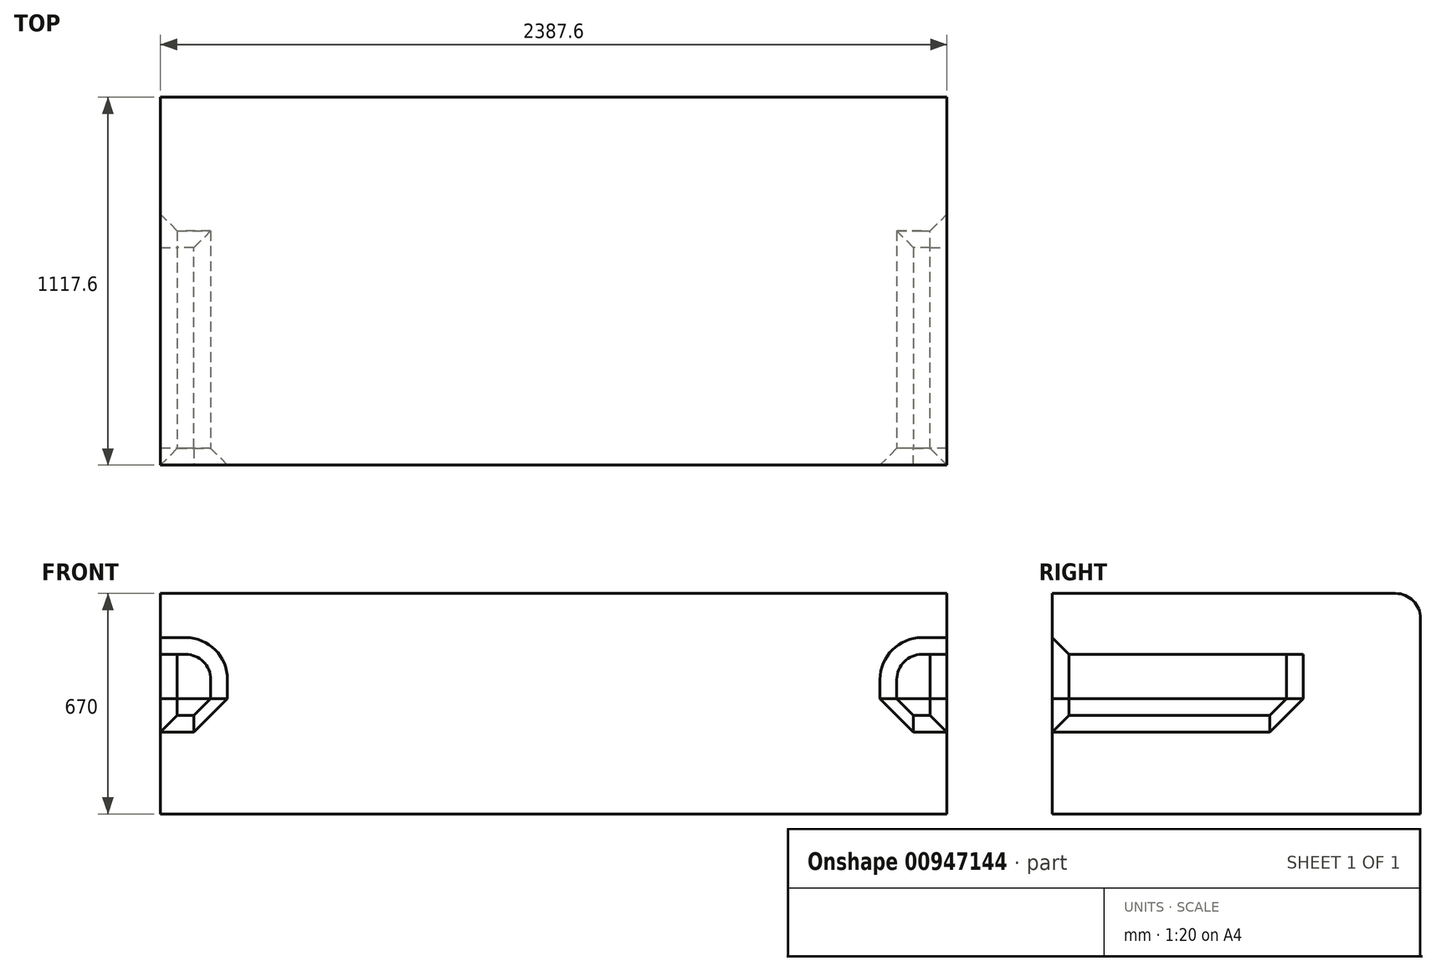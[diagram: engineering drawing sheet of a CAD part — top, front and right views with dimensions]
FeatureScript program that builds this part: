
annotation { "Feature Type Name" : "Feature", "Feature Type Description" : "" }
export const myFeature = defineFeature(function(context is Context, id is Id, definition is map)
    precondition{}
    {
        {
            var Q0;
            Q0=qCreatedBy(makeId("Top.planeOp"),FACE);
            var sketch = newSketch(context, id + "F0", { "sketchPlane" : qUnion([Q0])});
            skLineSegment(sketch, "E0.bottom", {"start": v(0, 0) * mm, "end": v(-2387.6, 0) * mm});
            skLineSegment(sketch, "E0.top", {"start": v(0, 1117.6) * mm, "end": v(-2387.6, 1117.6) * mm});
            skLineSegment(sketch, "E0.left", {"start": v(0, 0) * mm, "end": v(0, 1117.6) * mm});
            skLineSegment(sketch, "E0.right", {"start": v(-2387.6, 0) * mm, "end": v(-2387.6, 1117.6) * mm});
            skSolve(sketch);
        }
        {
            var Q0;
            Q0 = qSketchRegion(id + "F0", true);
            extrude(context, id + "F1", {"entities" : qUnion([Q0]), "flatOperationType" : FlatOperationType.REMOVE, "depth" : 670 * mm, "offsetDistance" : 25.4 * mm, "domain" : OperationDomain.MODEL});
        }
        {
            var Q0;
            Q0=makeQuery(id+"F1.opExtrude","SWEPT_FACE",FACE,{"disambiguationData":[OSD([sQuery(id+"F0.wireOp",EDGE,"E0.bottom")])]});
            var sketch = newSketch(context, id + "F2", { "sketchPlane" : qUnion([Q0])});
            skLineSegment(sketch, "E1.bottom", {"start": v(0, 300) * mm, "end": v(-2387.6, 300) * mm});
            skLineSegment(sketch, "E1.top", {"start": v(0, 670) * mm, "end": v(-2387.6, 670) * mm});
            skLineSegment(sketch, "E1.left", {"start": v(0, 300) * mm, "end": v(0, 670) * mm});
            skLineSegment(sketch, "E1.right", {"start": v(-2387.6, 300) * mm, "end": v(-2387.6, 670) * mm});
            skLineSegment(sketch, "E2.bottom", {"start": v(-2387.6, 670) * mm, "end": v(-2235.2, 670) * mm});
            skLineSegment(sketch, "E2.top", {"start": v(-2387.6, 300) * mm, "end": v(-2235.2, 300) * mm});
            skLineSegment(sketch, "E2.left", {"start": v(-2387.6, 670) * mm, "end": v(-2387.6, 300) * mm});
            skLineSegment(sketch, "E2.right", {"start": v(-2235.2, 485) * mm, "end": v(-2235.2, 300) * mm});
            skLineSegment(sketch, "E3.bottom", {"start": v(0, 670) * mm, "end": v(-152.4, 670) * mm});
            skLineSegment(sketch, "E3.top", {"start": v(0, 300) * mm, "end": v(-152.4, 300) * mm});
            skLineSegment(sketch, "E3.left", {"start": v(0, 670) * mm, "end": v(0, 300) * mm});
            skLineSegment(sketch, "E3.right", {"start": v(-152.4, 485) * mm, "end": v(-152.4, 300) * mm});
            skLineSegment(sketch, "E4", {"start": v(-2387.6, 485) * mm, "end": v(-2235.2, 485) * mm});
            skLineSegment(sketch, "E5", {"start": v(-152.4, 485) * mm, "end": v(0, 485) * mm});
            skSolve(sketch);
        }
        {
            var Q0;
            Q0=makeQuery(id+"F2.imprint","IMPRINT",FACE,{"disambiguationData":[TD([[makeQuery(id+"F2.imprint","IMPRINT",EDGE,{"derivedFrom":sQuery(id+"F2.wireOp",EDGE,"E1.bottom")}),-1.0]])]});
            extrude(context, id + "F3", {"entities" : qUnion([Q0]), "operationType" : NewBodyOperationType.REMOVE, "oppositeDirection" : true, "depth" : 711.2 * mm, "offsetDistance" : 25.4 * mm});
        }
        {
            var Q0;
            Q0=makeQuery(id+"F3.boolean.opBoolean","COPY",EDGE,{"derivedFrom":makeQuery(id+"F3.opExtrude","SWEPT_EDGE",EDGE,{"disambiguationData":[OSD([sQuery(id+"F2.wireOp",EDGE,"E2.right"),sQuery(id+"F2.wireOp",EDGE,"E4")])]})});
            var Q1;
            Q1=makeQuery(id+"F3.boolean.opBoolean","COPY",EDGE,{"derivedFrom":makeQuery(id+"F3.opExtrude","CAP_EDGE",EDGE,{"disambiguationData":[OSD([sQuery(id+"F2.wireOp",EDGE,"E1.top"),sQuery(id+"F2.wireOp",EDGE,"E2.bottom"),sQuery(id+"F2.wireOp",EDGE,"E3.bottom")])],"isStart":false})});
            var Q2;
            Q2=makeQuery(id+"F3.boolean.opBoolean","COPY",EDGE,{"derivedFrom":makeQuery(id+"F3.opExtrude","SWEPT_EDGE",EDGE,{"disambiguationData":[OSD([sQuery(id+"F2.wireOp",EDGE,"E3.right"),sQuery(id+"F2.wireOp",EDGE,"E5")])]})});
            var Q3;
            Q3=makeQuery(id+"F3.boolean.opBoolean","COPY",EDGE,{"derivedFrom":makeQuery(id+"F3.opExtrude","SWEPT_EDGE",EDGE,{"disambiguationData":[OSD([sQuery(id+"F2.wireOp",EDGE,"E3.left"),sQuery(id+"F2.wireOp",EDGE,"E5")])]})});
            var Q4;
            Q4=makeQuery(id+"F1.opExtrude","CAP_EDGE",EDGE,{"disambiguationData":[OSD([sQuery(id+"F0.wireOp",EDGE,"E0.top")])],"isStart":false});
            var Q5;
            Q5=makeQuery(id+"F3.boolean.opBoolean","COPY",EDGE,{"derivedFrom":makeQuery(id+"F3.opExtrude","SWEPT_EDGE",EDGE,{"disambiguationData":[OSD([sQuery(id+"F2.wireOp",EDGE,"E2.left"),sQuery(id+"F2.wireOp",EDGE,"E4")])]})});
            var Q6;
            Q6=makeQuery(id+"F3.boolean.opBoolean","COPY",EDGE,{"derivedFrom":makeQuery(id+"F3.opExtrude","CAP_EDGE",EDGE,{"disambiguationData":[OSD([sQuery(id+"F2.wireOp",EDGE,"E2.left")])],"isStart":false})});
            var Q7;
            Q7=makeQuery(id+"F3.boolean.opBoolean","COPY",EDGE,{"derivedFrom":makeQuery(id+"F3.opExtrude","CAP_EDGE",EDGE,{"disambiguationData":[OSD([sQuery(id+"F2.wireOp",EDGE,"E3.left")])],"isStart":false})});
            fillet(context, id + "F4", {"entities" : qUnion([Q0, Q1, Q2, Q3, Q4, Q5, Q6, Q7]), "radius" : 76.2 * mm, "tangentPropagation" : true, "allowEdgeOverflow" : false});
        }
        {
            var Q0;
            Q0=makeQuery(id+"F3.boolean.opBoolean","COPY",EDGE,{"derivedFrom":makeQuery(id+"F3.opExtrude","CAP_EDGE",EDGE,{"disambiguationData":[OSD([sQuery(id+"F2.wireOp",EDGE,"E1.bottom")])],"isStart":false})});
            var Q1;
            Q1=makeQuery(id+"F3.boolean.opBoolean","COPY",FACE,{"derivedFrom":makeQuery(id+"F3.opExtrude","SWEPT_FACE",FACE,{"disambiguationData":[OSD([sQuery(id+"F2.wireOp",EDGE,"E1.bottom")])]})});
            chamfer(context, id + "F5", {"entities" : qUnion([Q0, Q1]), "width" : 50.8 * mm, "tangentPropagation" : true});
        }
    });
